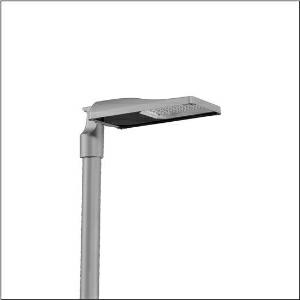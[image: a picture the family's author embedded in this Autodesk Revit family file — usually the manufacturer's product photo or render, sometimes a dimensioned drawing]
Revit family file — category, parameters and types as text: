
# Revit family: streetlight_sl_31_mini___st1_0a_5xh2d71b08ha_8b0a
name_source: partatom
category: Lighting Fixtures
units: mm (PartAtom-declared; Revit-internal decimal feet)

## family parameters
Cut with Voids When Loaded = No
Host = Face
Light Source = No
Part Type = Normal
Room Calculation Point = No
Round Connector Dimension = Use Diameter
Shared = No

## types (1)
- --- (1 x LED, 7470 lm, 68.3 W, 2200K)
    Apparent Load = 68 VA
    CIE Flux Codes = 37 72 97 100 100
    Color Rendering = 70
    Color Temperature = 2200K
    Default Elevation = 1800 mm
    Description = Streetlight SL 31 mini Easy, LST, Desk-Remote mast luminaire for post-top, side-entry; light control with lens of PMMA; light distribution: ST1.0a, direct asymmetric distribution, for standard-compliant lighting for roads and squares; LED: luminous flux: 7.470lm, light colour: 722, colour temperature: 2200K; luminous efficacy: 109,4lm/W; control: pre-setting: linear dimming characteristic, flexible luminous flux parameterisation, time-dependent luminous flux control, constant luminous flux control, power reduction, intelligent temperature release in ECG and LED module, overheat protection; luminaire housing, of diecast aluminium, SITECO metallic grey (DB 702S), corrosivity category C5 high according to DIN EN ISO 12944; cover of toughened safety glass, transparent, mast flange of diecast aluminium, SITECO metallic grey (DB 702S), spigot size: 76/60mm, mast flange included unmounted; cable length: 8,5m, connection cable pre-assembled; mains connection: 220..240V, AC, 50/60Hz; power consumption (at start of service life): 68,3W / (at end of service life): 74,8W / (with reduced operation 50%): 29,4W; protection rating (complete): IP66; insulation class (complete): insulation class II (safety insulation); impact resistance: IK10; certification: CE, ENEC, ENEC+, VDE, UKCA; permissible operating ambient temperature for outdoor applications: -40..+50°C; packaging unit: 1 piece

Light Distribution: ST1.0a
    Height = 76 mm
    Lamp = 1 x LED
    Lamp Light Flux = 7470 lm
    Lamp Power = 68.3 W
    Lamp count = 1
    Length = 547 mm
    Luminous efficacy = 109 lm/W
    Manufacturer = Siteco
    ModVariant = No
    Model = 5XH2D71B08HA
    Number of Poles = 1
    OnlyDefault = Yes
    Power Factor = 1
    Product Name = Streetlight SL 31 mini | ST1.0a
    Product group = mast luminaire | pylon top
    ProductGroupID = 6100
    Protection Class = Protection class II
    Protection Degree = IP 66
    RLX_Detail_Level = 1
    RLX_Emergency_Light_Flux = 0 lm
    RLX_Emergency_Type = 0
    RLX_Emergency_Type_DB = No
    RlxData = <blob elided: 39489 chars, md5=130aa52a>
    Socket = socket
    Standby Power = 0 W
    System Light Flux = 7470 lm
    System Power = 68 W
    Type Comments = factory setting: luminous flux: 100 % | dim-lin: 254 | 693 mA
    Type Image = l_1300326.jpg
    URL = http://relux.com
    VarID = @adj_009437
    Voltage = 0 V
    Weight = 0.00 kg
    Width = 265 mm

## geometry (parser evidence)
native form markers: Blend x4, Sweep x8
no freeform markers — native parametric forms only
